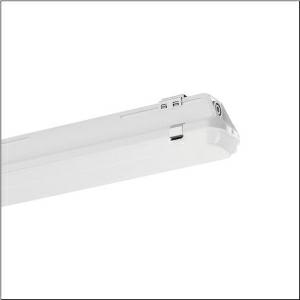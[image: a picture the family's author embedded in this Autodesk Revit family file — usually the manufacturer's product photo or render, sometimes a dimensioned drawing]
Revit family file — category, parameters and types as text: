
# Revit family: monsun_r__12_51fp10fp460h_de62
name_source: partatom
category: Lighting Fixtures
units: mm (PartAtom-declared; Revit-internal decimal feet)

## family parameters
Cut with Voids When Loaded = No
Host = Face
Light Source = No
Part Type = Normal
Room Calculation Point = No
Round Connector Dimension = Use Diameter
Shared = No

## types (1)
- --- (1 x LED, 6050 lm, 34.6 W, 4000K)
    Apparent Load = 35 VA
    CIE Flux Codes = 47 77 93 94 100
    Color Rendering = 80
    Color Temperature = 4000K
    Default Elevation = 1800 mm
    Description = Monsun® 12, damp-proof luminaire, chain hanger, primary optical cover: enclosure, of PMMA, light emission: direct distribution, primary light characteristic: symmetric, installation type: suspended mounting, surface-mounted, horizontal mounting, vertical mounting, LED, rated luminous flux: 6.050lm, luminous efficacy: 175lm/W, light colour: 840, colour temperature: 4000K, control gear: ECG DALI, with terminal, 5-pole, max. 2.5mm², mains connection: 220..240V, AC, 50/60Hz, start of lifetime: 35W, end of lifetime: 39W, luminaire housing, of glass-fibre reinforced polyester, uncoated, bright grey, length: 1.590mm, width: 90mm, height: 88mm, clip for enclosure, of stainless steel (V2A), ceiling mounting element, of stainless steel (V2A), chain hanger, of stainless steel (V2A), protection rating (complete): IP66, insulation class (complete): insulation class I (protective earthing), certification: CE, ENEC, VDE, protection symbol: D, impact resistance: IK04, permissible operating ambient temperature: -25..+40°C, standard: EN 50419, EN 60598-2-1, no direct snow, no direct sun, no direct rain, for indoor or canopied outdoor use, corresponds to IFS (International Featured Standards) requirements for safety and quality in the food industry, for animal farming (ammonia tested): for use in cowhouse, pig house, horse-stables... (not for use in poultry stables), AT max for animal farming = 40°C, packaging unit: 1 piece
    Height = 89 mm
    Lamp = 1 x LED
    Lamp Light Flux = 6050 lm
    Lamp Power = 34.6 W
    Lamp count = 1
    Length = 1590 mm
    Luminous efficacy = 175 lm/W
    Manufacturer = Siteco
    ModVariant = No
    Model = 51FP10FP460H
    Mounting Place = Ceiling
    Mounting Type = Pendant
    Number of Poles = 1
    OnlyDefault = Yes
    Power Factor = 1
    Product Name = Monsun® 12
    Product group = damp-proof luminaire | ceiling pendant
    ProductGroupID = 908
    Protection Class = Protection class I
    Protection Degree = IP 66
    RLX_Detail_Level = 1
    RlxData = <blob elided: 92029 chars, md5=5ca3d5a9>
    Socket = socket
    Standby Power = 0 W
    System Light Flux = 6050 lm
    System Power = 35 W
    Type Comments = factory setting: luminous flux: 100 % | dim-lin: 254 | 232 mA
    Type Image = l_1004748.jpg
    URL = http://relux.com
    VarID = @adj_136381
    Voltage = 0 V
    Weight = 0.00 kg
    Width = 90 mm

## geometry (parser evidence)
native form markers: Blend x4, Sweep x11
no freeform markers — native parametric forms only
